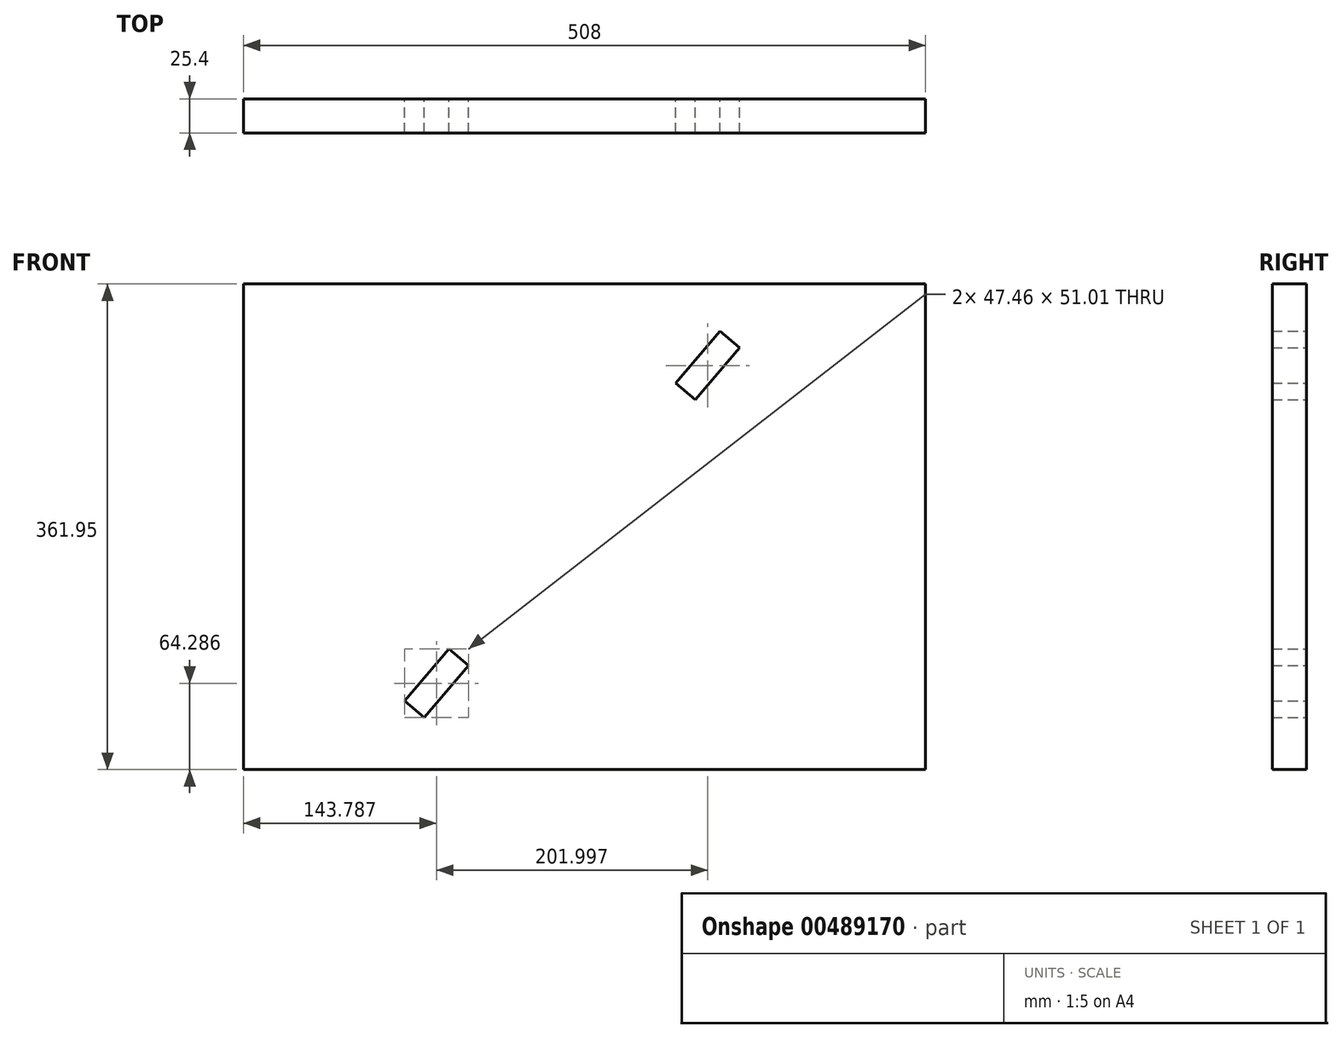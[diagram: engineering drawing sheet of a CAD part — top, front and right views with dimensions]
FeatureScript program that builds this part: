
annotation { "Feature Type Name" : "Feature", "Feature Type Description" : "" }
export const myFeature = defineFeature(function(context is Context, id is Id, definition is map)
    precondition{}
    {
        {
            var Q0;
            Q0=qCreatedBy(makeId("Front.planeOp"),FACE);
            var sketch = newSketch(context, id + "F0", { "sketchPlane" : qUnion([Q0])});
            skLineSegment(sketch, "E0.bottom", {"start": v(-319.09, 172.63) * mm, "end": v(188.91, 172.63) * mm});
            skLineSegment(sketch, "E0.top", {"start": v(-319.09, -189.32) * mm, "end": v(188.91, -189.32) * mm});
            skLineSegment(sketch, "E0.left", {"start": v(-319.09, 172.63) * mm, "end": v(-319.09, -189.32) * mm});
            skLineSegment(sketch, "E0.right", {"start": v(188.91, 172.63) * mm, "end": v(188.91, -189.32) * mm});
            skLineSegment(sketch, "E1.bottom", {"start": v(-319.09, -189.32) * mm, "end": v(-242.89, -189.32) * mm});
            skLineSegment(sketch, "E1.top", {"start": v(-319.09, -208.37) * mm, "end": v(-242.89, -208.37) * mm});
            skLineSegment(sketch, "E1.left", {"start": v(-319.09, -189.32) * mm, "end": v(-319.09, -208.37) * mm});
            skLineSegment(sketch, "E1.right", {"start": v(-242.89, -189.32) * mm, "end": v(-242.89, -208.37) * mm});
            skLineSegment(sketch, "E2.bottom", {"start": v(188.91, -189.32) * mm, "end": v(112.71, -189.32) * mm});
            skLineSegment(sketch, "E2.top", {"start": v(188.91, -208.37) * mm, "end": v(112.71, -208.37) * mm});
            skLineSegment(sketch, "E2.left", {"start": v(188.91, -189.32) * mm, "end": v(188.91, -208.37) * mm});
            skLineSegment(sketch, "E2.right", {"start": v(112.71, -189.32) * mm, "end": v(112.71, -208.37) * mm});
            skLineSegment(sketch, "E3", {"start": v(35.93, 137.3) * mm, "end": v(50.42, 124.93) * mm});
            skLineSegment(sketch, "E4", {"start": v(50.42, 124.93) * mm, "end": v(17.46, 86.28) * mm});
            skLineSegment(sketch, "E5", {"start": v(17.46, 86.28) * mm, "end": v(2.96, 98.65) * mm});
            skLineSegment(sketch, "E6", {"start": v(2.96, 98.65) * mm, "end": v(35.93, 137.3) * mm});
            skLineSegment(sketch, "E7", {"start": v(-151.57, -111.9) * mm, "end": v(-184.54, -150.54) * mm});
            skLineSegment(sketch, "E8", {"start": v(-166.07, -99.53) * mm, "end": v(-199.03, -138.18) * mm});
            skLineSegment(sketch, "E9", {"start": v(-151.57, -111.9) * mm, "end": v(-166.07, -99.53) * mm});
            skLineSegment(sketch, "E10", {"start": v(-199.03, -138.18) * mm, "end": v(-184.54, -150.54) * mm});
            skSolve(sketch);
        }
        {
            var Q0;
            Q0=makeQuery(id+"F0.imprint","IMPRINT",FACE,{"disambiguationData":[TD([[makeQuery(id+"F0.imprint","IMPRINT",EDGE,{"derivedFrom":sQuery(id+"F0.wireOp",EDGE,"E0.bottom")}),-1.0]])]});
            var Q1;
            Q1=makeQuery(id+"F0.imprint","IMPRINT",FACE,{"disambiguationData":[TD([[makeQuery(id+"F0.imprint","IMPRINT",EDGE,{"derivedFrom":sQuery(id+"F0.wireOp",EDGE,"E1.bottom")}),-1.0]])]});
            var Q2;
            Q2=makeQuery(id+"F0.imprint","IMPRINT",FACE,{"disambiguationData":[TD([[makeQuery(id+"F0.imprint","IMPRINT",EDGE,{"derivedFrom":sQuery(id+"F0.wireOp",EDGE,"E2.bottom")}),1.0]])]});
            extrude(context, id + "F1", {"entities" : qUnion([Q0, Q1, Q2]), "depth" : 25.4 * mm, "offsetDistance" : 25.4 * mm});
        }
    });
